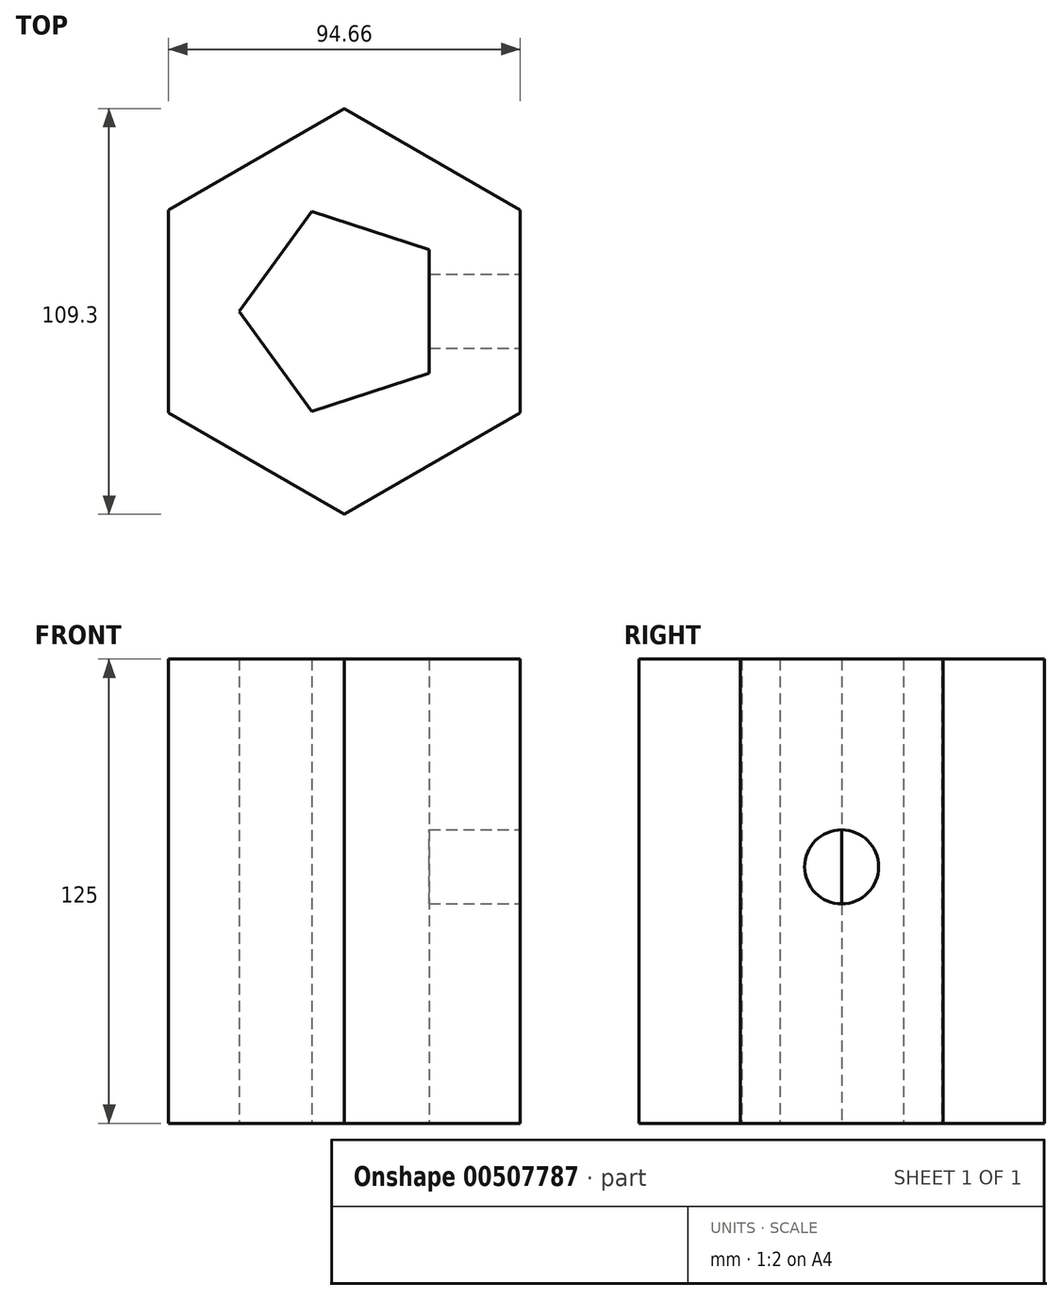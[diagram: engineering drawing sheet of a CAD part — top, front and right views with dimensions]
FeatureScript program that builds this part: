
annotation { "Feature Type Name" : "Feature", "Feature Type Description" : "" }
export const myFeature = defineFeature(function(context is Context, id is Id, definition is map)
    precondition{}
    {
        {
            var Q0;
            Q0=qCreatedBy(makeId("Top.planeOp"),FACE);
            var sketch = newSketch(context, id + "F0", { "sketchPlane" : qUnion([Q0])});
            skCircle(sketch, "E0.cCircle", {"center": v(0, 0) * mm, "radius": 54.65 * mm, "construction": true});
            skLineSegment(sketch, "E0.0", {"start": v(0, 54.65) * mm, "end": v(47.33, 27.33) * mm});
            skLineSegment(sketch, "E0.1", {"start": v(47.33, 27.33) * mm, "end": v(47.33, -27.33) * mm});
            skLineSegment(sketch, "E0.2", {"start": v(47.33, -27.33) * mm, "end": v(0, -54.65) * mm});
            skLineSegment(sketch, "E0.3", {"start": v(0, -54.65) * mm, "end": v(-47.33, -27.33) * mm});
            skLineSegment(sketch, "E0.4", {"start": v(-47.33, -27.33) * mm, "end": v(-47.33, 27.33) * mm});
            skLineSegment(sketch, "E0.5", {"start": v(-47.33, 27.33) * mm, "end": v(0, 54.65) * mm});
            skCircle(sketch, "E1.cCircle", {"center": v(0, 0) * mm, "radius": 28.3 * mm, "construction": true});
            skLineSegment(sketch, "E1.0", {"start": v(-28.3, 0) * mm, "end": v(-8.75, 26.92) * mm});
            skLineSegment(sketch, "E1.1", {"start": v(-8.75, 26.92) * mm, "end": v(22.9, 16.63) * mm});
            skLineSegment(sketch, "E1.2", {"start": v(22.9, 16.63) * mm, "end": v(22.9, -16.63) * mm});
            skLineSegment(sketch, "E1.3", {"start": v(22.9, -16.63) * mm, "end": v(-8.75, -26.92) * mm});
            skLineSegment(sketch, "E1.4", {"start": v(-8.75, -26.92) * mm, "end": v(-28.3, 0) * mm});
            skSolve(sketch);
        }
        {
            var Q0;
            Q0=makeQuery(id+"F0.imprint","IMPRINT",FACE,{"disambiguationData":[TD([[makeQuery(id+"F0.imprint","IMPRINT",EDGE,{"derivedFrom":sQuery(id+"F0.wireOp",EDGE,"E0.0")}),-1.0]])]});
            extrude(context, id + "F1", {"entities" : qUnion([Q0]), "depth" : 125 * mm});
        }
        {
            var Q0;
            Q0=makeQuery(id+"F1.opExtrude","SWEPT_FACE",FACE,{"disambiguationData":[OSD([sQuery(id+"F0.wireOp",EDGE,"E0.1")])]});
            var sketch = newSketch(context, id + "F2", { "sketchPlane" : qUnion([Q0])});
            skCircle(sketch, "E2", {"center": v(0, 69.05) * mm, "radius": 9.97 * mm});
            skSolve(sketch);
        }
        {
            var Q0;
            Q0=makeQuery(id+"F2.imprint","IMPRINT",FACE,{"disambiguationData":[TD([[makeQuery(id+"F2.imprint","IMPRINT",EDGE,{"derivedFrom":sQuery(id+"F2.wireOp",EDGE,"E2")}),1.0]])]});
            extrude(context, id + "F3", {"entities" : qUnion([Q0]), "operationType" : NewBodyOperationType.REMOVE, "oppositeDirection" : true, "depth" : 25 * mm});
        }
    });
